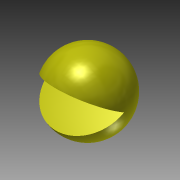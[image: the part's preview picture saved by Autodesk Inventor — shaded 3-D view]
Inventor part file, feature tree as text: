
AUTODESK INVENTOR PART (.ipt)
format: ipt  version: 2015 (Build 190159000, 159)  size: 116,224 bytes
history: native  units: in
note: dims shown in document units (in); Inventor stores cm internally (conversion verified against a paired STEP export)
features: sketch x2, revolve x1, extrude x1
ambient origin geometry x8: Origin, YZ Plane, XZ Plane, XY Plane, X Axis, Y Axis, Z Axis, Center Point
bodies: Solid1 (feature_tree)
feature tree (4):
  revolve  "Revolution1"  Angle=90.0deg
  extrude  "Extrusion1"  TaperAngle=30.0deg  [1 undecoded]
  sketch  "Sketch1"  dims[d0=1.1in d1=90.0deg]
  sketch  "Sketch3"  dims[d2=30.0deg d3=30.0deg d4=2.0in d5=0.0in]
note: 1 required parameter value undecoded (feature->parameter linkage not recoverable at this tier; creation-order binding heuristic only, values carry confidence <= 0.55)
